# Revit family: QF_MACOM_BM91C-2M
name_source: partatom
category: Equipamento especial
units: mm (PartAtom-declared; Revit-internal decimal feet)

## family parameters
Com base no plano de trabalho = Não
Compartilhado = Não
Corte com vazios quando carregada = Não
Cota do conector redondo = Utilizar diâmetro
Número OmniClass = 23.40.40.14.17.11
Ponto de cálculo do ambiente = Não
Sempre na vertical = Sim
Tipo de parte = Normal
Título OmniClass = Cookers, Ovens, Stoves

## types (1)
- BM91C-2M
    Capacity in Litres = 32,7 L
    Cycle = 60 Hz
    Depth = 972 mm
    Descrição = BANHO-MARIA ELETRICO 900HP MACOM 220V MONOF - 450X972X265MM
    Elec Connection Height = 50 mm
    Electric Power = 2800 W
    Elevação padrão = 0 mm
    Fabricante = MACOM
    Height = 286 mm
    Ingress Protection Code = IP 22
    Length = 450 mm
    Modelo = BM91C-2M
    URL = https://www.acosmacom.com.br
    Volts = 220 V
    Volume = 0,13 m³
    Weight = 25 kg
    Work Temperature = 20º C to 85° C

## geometry (parser evidence)
native form markers: Sweep x6
no freeform markers — native parametric forms only
